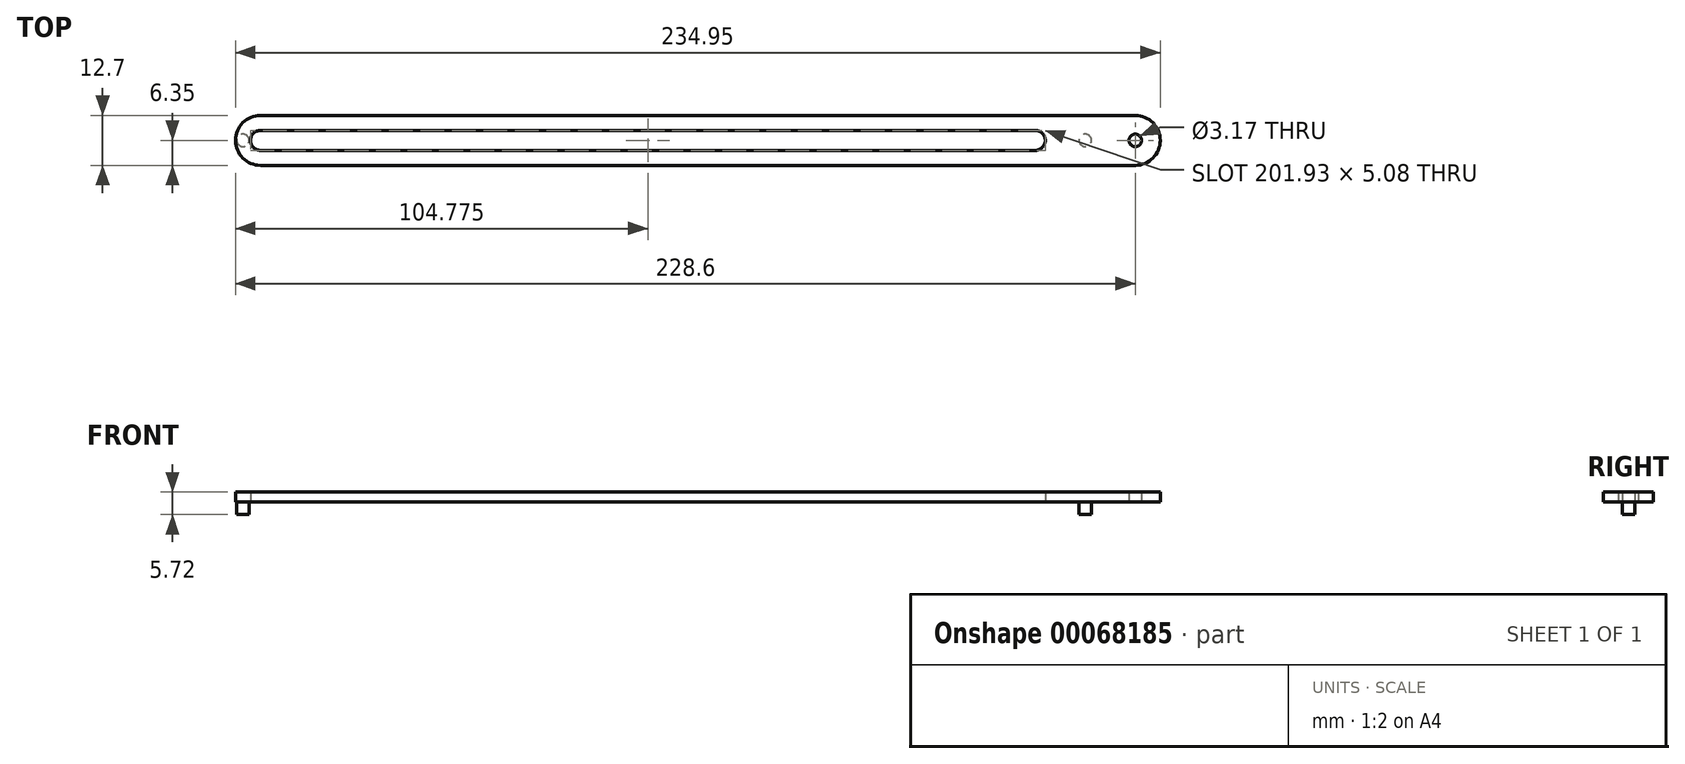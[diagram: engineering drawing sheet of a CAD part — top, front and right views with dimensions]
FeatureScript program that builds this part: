
annotation { "Feature Type Name" : "Feature", "Feature Type Description" : "" }
export const myFeature = defineFeature(function(context is Context, id is Id, definition is map)
    precondition{}
    {
        {
            var Q0;
            Q0=qCreatedBy(makeId("Top.planeOp"),FACE);
            var sketch = newSketch(context, id + "F0", { "sketchPlane" : qUnion([Q0])});
            skLineSegment(sketch, "E0.bottom", {"start": v(0, 0) * mm, "end": v(222.25, 0) * mm});
            skLineSegment(sketch, "E0.top", {"start": v(0, 12.7) * mm, "end": v(222.25, 12.7) * mm});
            skArc(sketch, "E1", {"start": v(222.25, 0) * mm, "mid": v(228.6, 6.35) * mm, "end": v(222.25, 12.7) * mm});
            skArc(sketch, "E2", {"start": v(0, 12.7) * mm, "mid": v(-6.35, 6.35) * mm, "end": v(0, 0) * mm});
            skLineSegment(sketch, "E3.0", {"start": v(0, 3.81) * mm, "end": v(196.85, 3.81) * mm});
            skLineSegment(sketch, "E4.0", {"start": v(0, 8.9) * mm, "end": v(196.85, 8.9) * mm});
            skArc(sketch, "E5", {"start": v(0, 8.9) * mm, "mid": v(-2.54, 6.35) * mm, "end": v(0, 3.81) * mm});
            skArc(sketch, "E6", {"start": v(196.85, 3.81) * mm, "mid": v(199.4, 6.35) * mm, "end": v(196.85, 8.9) * mm});
            skCircle(sketch, "E7", {"center": v(222.25, 6.35) * mm, "radius": 1.59 * mm});
            skSolve(sketch);
        }
        {
            var Q0;
            Q0=makeQuery(id+"F0.imprint","IMPRINT",FACE,{"disambiguationData":[TD([[makeQuery(id+"F0.imprint","IMPRINT",EDGE,{"derivedFrom":sQuery(id+"F0.wireOp",EDGE,"E0.bottom")}),1.0]])]});
            extrude(context, id + "F1", {"entities" : qUnion([Q0]), "depth" : 2.54 * mm});
        }
        {
            var Q0;
            Q0=makeQuery(id+"F1.opExtrude","CAP_FACE",FACE,{"disambiguationData":[OSD([sQuery(id+"F0.wireOp",EDGE,"E0.bottom"),sQuery(id+"F0.wireOp",EDGE,"E0.top"),sQuery(id+"F0.wireOp",EDGE,"E1"),sQuery(id+"F0.wireOp",EDGE,"E2"),sQuery(id+"F0.wireOp",EDGE,"E3.0"),sQuery(id+"F0.wireOp",EDGE,"E4.0"),sQuery(id+"F0.wireOp",EDGE,"E5"),sQuery(id+"F0.wireOp",EDGE,"E6"),sQuery(id+"F0.wireOp",EDGE,"E7")])],"isStart":true});
            var sketch = newSketch(context, id + "F2", { "sketchPlane" : qUnion([Q0])});
            skCircle(sketch, "E8", {"center": v(209.55, -6.35) * mm, "radius": 1.59 * mm});
            skCircle(sketch, "E9", {"center": v(-4.44, -6.35) * mm, "radius": 1.59 * mm});
            skLineSegment(sketch, "E10", {"start": v(-2.54, -6.35) * mm, "end": v(-6.35, -6.35) * mm, "construction": true});
            skPoint(sketch, "E11", {"position": v(222.25, -6.35) * mm});
            skSolve(sketch);
        }
        {
            var Q0;
            Q0 = qSketchRegion(id + "F2", true);
            extrude(context, id + "F3", {"entities" : qUnion([Q0]), "operationType" : NewBodyOperationType.ADD, "depth" : 3.17 * mm});
        }
    });
